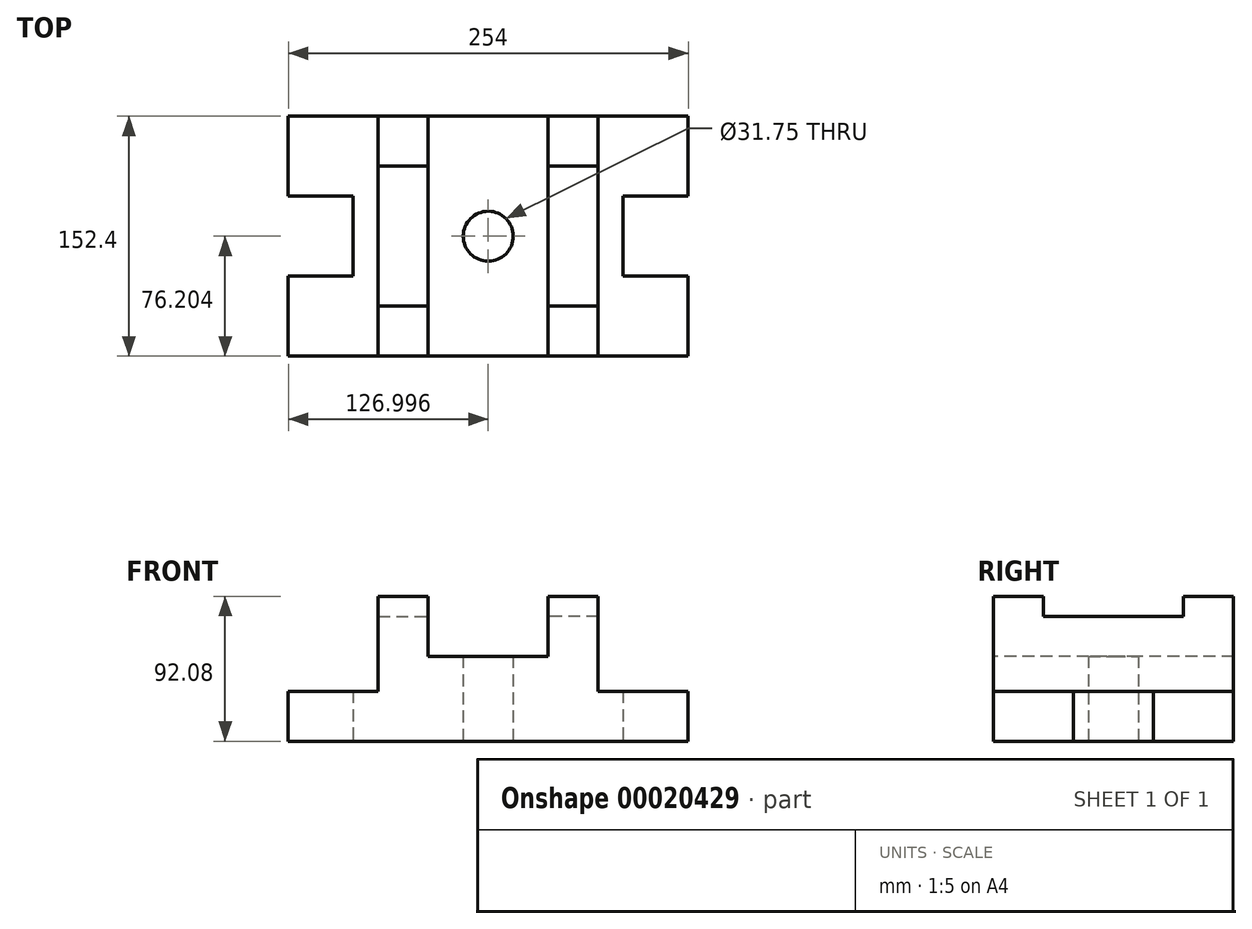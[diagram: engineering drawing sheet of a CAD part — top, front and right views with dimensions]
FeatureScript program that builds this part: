
annotation { "Feature Type Name" : "Feature", "Feature Type Description" : "" }
export const myFeature = defineFeature(function(context is Context, id is Id, definition is map)
    precondition{}
    {
        {
            var Q0;
            Q0=qCreatedBy(makeId("Top.planeOp"),FACE);
            var sketch = newSketch(context, id + "F0", { "sketchPlane" : qUnion([Q0])});
            skLineSegment(sketch, "E0", {"start": v(-126.54, 78.85) * mm, "end": v(-37.64, 78.85) * mm});
            skLineSegment(sketch, "E1", {"start": v(-85.27, 2.65) * mm, "end": v(-85.27, 28.05) * mm});
            skLineSegment(sketch, "E2", {"start": v(-85.27, 28.05) * mm, "end": v(-126.54, 28.05) * mm});
            skLineSegment(sketch, "E3", {"start": v(-126.54, 28.05) * mm, "end": v(-126.54, 78.85) * mm});
            skLineSegment(sketch, "E4", {"start": v(-69.4, 78.85) * mm, "end": v(-69.4, 2.65) * mm});
            skLineSegment(sketch, "E5", {"start": v(-37.64, 78.85) * mm, "end": v(-37.64, 2.65) * mm});
            skArc(sketch, "E6", {"start": v(0.46, 18.53) * mm, "mid": v(-10.77, 13.88) * mm, "end": v(-15.42, 2.65) * mm});
            skLineSegment(sketch, "E7", {"start": v(-69.4, 47.1) * mm, "end": v(-37.64, 47.1) * mm});
            skLineSegment(sketch, "E8", {"start": v(-85.27, 2.65) * mm, "end": v(0.46, 2.65) * mm});
            skLineSegment(sketch, "E9", {"start": v(0.46, 78.85) * mm, "end": v(0.46, 2.65) * mm});
            skPoint(sketch, "E10.orphan", {"position": v(38.56, 78.85) * mm});
            skPoint(sketch, "E11.start.orphan", {"position": v(38.56, 47.1) * mm});
            skPoint(sketch, "E12.trimOffspring.start.orphan", {"position": v(70.3, 78.85) * mm});
            skPoint(sketch, "E13.start.orphan", {"position": v(127.46, 78.85) * mm});
            skPoint(sketch, "E14.end.orphan", {"position": v(86.18, 28.05) * mm});
            skPoint(sketch, "E14.start.orphan", {"position": v(127.46, 28.05) * mm});
            skPoint(sketch, "E15.start.orphan", {"position": v(86.18, -22.75) * mm});
            skPoint(sketch, "E16.start.orphan", {"position": v(127.46, -22.75) * mm});
            skPoint(sketch, "E17.start.orphan", {"position": v(38.56, -41.8) * mm});
            skPoint(sketch, "E18.start.orphan", {"position": v(-69.4, -41.8) * mm});
            skPoint(sketch, "E19.trimOffspring.start.orphan", {"position": v(-37.64, -41.8) * mm});
            skPoint(sketch, "E20.start.orphan", {"position": v(-69.4, -73.55) * mm});
            skPoint(sketch, "E21.start.orphan", {"position": v(-126.54, -22.75) * mm});
            skPoint(sketch, "E22.orphan", {"position": v(-85.27, -22.75) * mm});
            skLineSegment(sketch, "E23", {"start": v(-37.64, 78.85) * mm, "end": v(0.46, 78.85) * mm});
            skSolve(sketch);
        }
        {
            var Q0;
            {var subQ3=sQuery(id+"F0.wireOp",EDGE,"E1");Q0=makeQuery(id+"F0.imprint","IMPRINT",FACE,{"disambiguationData":[TD([[makeQuery(id+"F0.imprint","IMPRINT",EDGE,{"derivedFrom":subQ3}),-1.0]])]});}
            extrude(context, id + "F1", {"entities" : qUnion([Q0]), "depth" : 31.75 * mm});
        }
        {
            var Q0;
            {var subQ0=sQuery(id+"F0.wireOp",EDGE,"E7");Q0=makeQuery(id+"F0.imprint","IMPRINT",FACE,{"disambiguationData":[TD([[makeQuery(id+"F0.imprint","IMPRINT",EDGE,{"derivedFrom":subQ0}),1.0]])]});}
            extrude(context, id + "F2", {"entities" : qUnion([Q0]), "operationType" : NewBodyOperationType.ADD, "depth" : 92.07 * mm});
        }
        {
            var Q0;
            {var subQ2=sQuery(id+"F0.wireOp",EDGE,"E6");Q0=makeQuery(id+"F0.imprint","IMPRINT",FACE,{"disambiguationData":[TD([[makeQuery(id+"F0.imprint","IMPRINT",EDGE,{"derivedFrom":subQ2}),-1.0]])]});}
            extrude(context, id + "F3", {"entities" : qUnion([Q0]), "operationType" : NewBodyOperationType.ADD, "depth" : 53.97 * mm});
        }
        {
            var Q0;
            {var subQ5=sQuery(id+"F0.wireOp",EDGE,"E7");Q0=makeQuery(id+"F0.imprint","IMPRINT",FACE,{"disambiguationData":[TD([[makeQuery(id+"F0.imprint","IMPRINT",EDGE,{"derivedFrom":subQ5}),-1.0]])]});}
            extrude(context, id + "F4", {"entities" : qUnion([Q0]), "operationType" : NewBodyOperationType.ADD, "depth" : 79.38 * mm});
        }
        {
            var Q0;
            Q0=makeQuery(id+"F1.opExtrude","SWEPT_BODY",BODY,{"disambiguationData":[OSD([sQuery(id+"F0.wireOp",EDGE,"E0"),sQuery(id+"F0.wireOp",EDGE,"E1"),sQuery(id+"F0.wireOp",EDGE,"E2"),sQuery(id+"F0.wireOp",EDGE,"E3"),sQuery(id+"F0.wireOp",EDGE,"E4"),sQuery(id+"F0.wireOp",EDGE,"E8")])]});
            var Q1;
            {var subQ0=sQuery(id+"F0.wireOp",EDGE,"E8");Q1=makeQuery(id+"F4.boolean.opBoolean","MERGE",FACE,{"derivedFrom":[makeQuery(id+"F1.opExtrude","SWEPT_FACE",FACE,{"disambiguationData":[OSD([subQ0])]}),makeQuery(id+"F3.opExtrude","SWEPT_FACE",FACE,{"disambiguationData":[OSD([subQ0])]}),makeQuery(id+"F4.opExtrude","SWEPT_FACE",FACE,{"disambiguationData":[OSD([subQ0])]})]});}
            mirror(context, id + "F5", {"operationType" : NewBodyOperationType.ADD, "entities" : qUnion([Q0]), "mirrorPlane" : qUnion([Q1])});
        }
        {
            var Q0;
            Q0=makeQuery(id+"F1.opExtrude","SWEPT_BODY",BODY,{"disambiguationData":[OSD([sQuery(id+"F0.wireOp",EDGE,"E0"),sQuery(id+"F0.wireOp",EDGE,"E1"),sQuery(id+"F0.wireOp",EDGE,"E2"),sQuery(id+"F0.wireOp",EDGE,"E3"),sQuery(id+"F0.wireOp",EDGE,"E4"),sQuery(id+"F0.wireOp",EDGE,"E8")])]});
            var Q1;
            Q1=makeQuery(id+"F5.opPattern","COPY",FACE,{"derivedFrom":makeQuery(id+"F3.opExtrude","SWEPT_FACE",FACE,{"disambiguationData":[OSD([sQuery(id+"F0.wireOp",EDGE,"E9")])]}),"instanceName":"1"});
            mirror(context, id + "F6", {"operationType" : NewBodyOperationType.ADD, "entities" : qUnion([Q0]), "mirrorPlane" : qUnion([Q1])});
        }
    });
